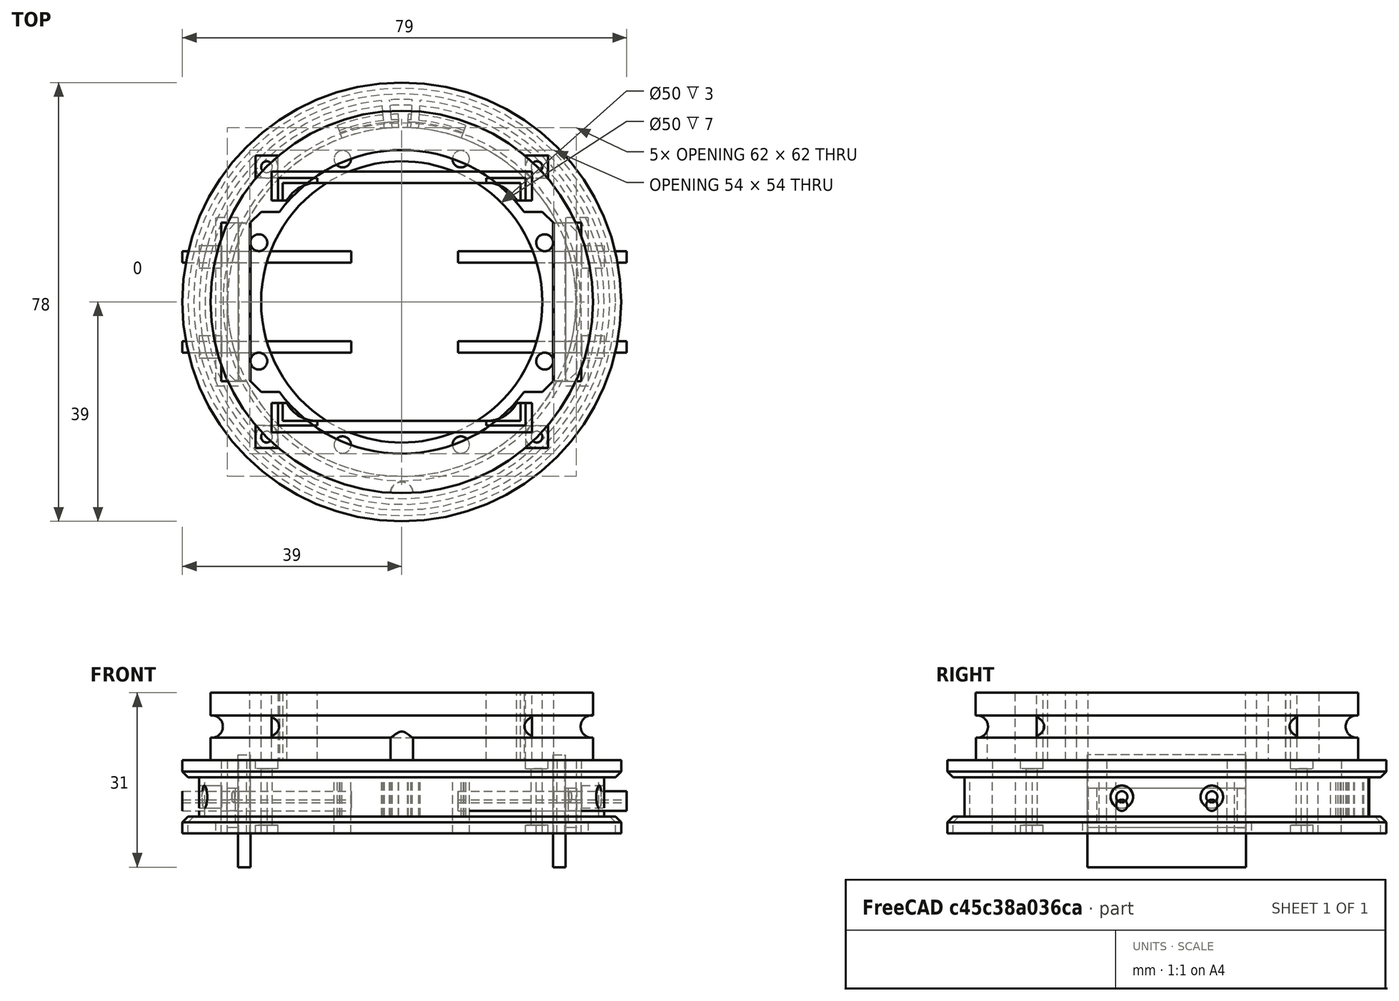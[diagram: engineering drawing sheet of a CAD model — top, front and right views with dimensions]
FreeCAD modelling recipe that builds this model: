
FCSTD DOCUMENT  (FreeCAD 0.19R24276 (Git))
Label: G-mini_encoder-ring_008
License: All rights reserved
LicenseURL: http://en.wikipedia.org/wiki/All_rights_reserved
objects: Part::Cylinder×73, Part::Box×67, Part::Cut×61, Part::Compound×53, Part::FeaturePython×11, Part::Chamfer×8, Mesh::Feature×5, Part::Torus×2
note: 275 computed .brp shape members not serialized (recipe doc carries the construction recipe); baked Part::Feature solids carry a one-line shape summary decoded from their .brp

FEATURE [Part::FeaturePython] Tube035  # WARN: FeaturePython — macro-defined, semantics opaque (R4)
  AttacherType = Attacher::AttachEngine3D
  Height = 2
  InnerRadius = 31
  OuterRadius = 39
  Placement = pos=(17,-103,10) rot=(1,0,0;1.5708rad)
FEATURE [Part::Box] Box850  label="Krychle849"
  AttacherType = Attacher::AttachEngine3D
  Height = 28
  Length = 2
  Placement = pos=(-14.1,-111,-4) rot=(0,0,1;0rad)
  Width = 7
FEATURE [Part::Box] Box851  label="Krychle850"
  AttacherType = Attacher::AttachEngine3D
  Height = 30
  Length = 4
  Placement = pos=(-16.1,-105,-5) rot=(0,0,1;0rad)
  Width = 2
FEATURE [Part::Box] Box852  label="Krychle851"
  AttacherType = Attacher::AttachEngine3D
  Height = 28.2
  Length = 2.2
  Placement = pos=(-12.1,-111,-4.1) rot=(0,0,1;0rad)
  Width = 10
FEATURE [Part::Cut] Cut807
  Base = -> Tube035
  Tool = -> Box852
FEATURE [Part::Compound] Compound985
  Links = -> [Box851,Cut807]
FEATURE [Part::Cylinder] Cylinder2203  label="Válec2203"
  Angle = 360
  AttacherType = Attacher::AttachEngine3D
  Height = 20
  Placement = pos=(-17,-108,2) rot=(0,1,0;1.5708rad)
  Radius = 1
FEATURE [Part::Cylinder] Cylinder2204  label="Válec2204"
  Angle = 360
  AttacherType = Attacher::AttachEngine3D
  Height = 20
  Placement = pos=(-17,-108,18) rot=(0,1,0;1.5708rad)
  Radius = 1
FEATURE [Part::Compound] Compound986
  Links = -> [Cylinder2203,Cylinder2204]
FEATURE [Part::Cut] Cut811
  Base = -> Box850
  Tool = -> Compound986
FEATURE [Part::Chamfer] Chamfer069
  Base = -> Cut811
  Edges = 2 edges r=1.5: [Edge2,Edge3]
FEATURE [Part::Box] Box853  label="Krychle852"
  AttacherType = Attacher::AttachEngine3D
  Height = 28.2
  Length = 2.2
  Placement = pos=(43.9,-111,-4.1) rot=(0,0,1;0rad)
  Width = 10
FEATURE [Part::Cut] Cut810
  Base = -> Compound985
  Tool = -> Box853
FEATURE [Part::Box] Box855  label="Krychle854"
  AttacherType = Attacher::AttachEngine3D
  Height = 28
  Length = 2
  Placement = pos=(46.1,-111,-4) rot=(0,0,1;0rad)
  Width = 7
FEATURE [Part::Box] Box856  label="Krychle855"
  AttacherType = Attacher::AttachEngine3D
  Height = 30
  Length = 4
  Placement = pos=(46.1,-105,-5) rot=(0,0,1;0rad)
  Width = 2
FEATURE [Part::Cylinder] Cylinder2205  label="Válec2205"
  Angle = 360
  AttacherType = Attacher::AttachEngine3D
  Height = 20
  Placement = pos=(32,-108,2) rot=(0,1,0;1.5708rad)
  Radius = 1
FEATURE [Part::Cylinder] Cylinder2206  label="Válec2206"
  Angle = 360
  AttacherType = Attacher::AttachEngine3D
  Height = 20
  Placement = pos=(32,-108,18) rot=(0,1,0;1.5708rad)
  Radius = 1
FEATURE [Part::Compound] Compound988
  Links = -> [Cylinder2205,Cylinder2206]
FEATURE [Part::Cut] Cut809
  Base = -> Box855
  Tool = -> Compound988
FEATURE [Part::Chamfer] Chamfer068
  Base = -> Cut809
  Edges = 2 edges r=1.5: [Edge11,Edge13]
FEATURE [Part::Compound] Compound989
  Links = -> [Chamfer069,Chamfer068,Cut810]
FEATURE [Part::Compound] Compound990  label="Wrist_halo-cover"
  Links = -> [Box856,Compound989]
  Placement = pos=(17,10,-111) rot=(0,0.707107,-0.707107;3.14159rad)
FEATURE [Part::FeaturePython] Tube084  # WARN: FeaturePython — macro-defined, semantics opaque (R4)
  AttacherType = Attacher::AttachEngine3D
  Height = 7
  InnerRadius = 25
  OuterRadius = 35
  Placement = pos=(0,0,3) rot=(0,0,1;0rad)
FEATURE [Part::FeaturePython] Tube093  # WARN: FeaturePython — macro-defined, semantics opaque (R4)
  AttacherType = Attacher::AttachEngine3D
  Height = 7
  InnerRadius = 31
  OuterRadius = 32.4
  Placement = pos=(0,0,-22) rot=(0,0,1;0rad)
FEATURE [Part::FeaturePython] Tube094  # WARN: FeaturePython — macro-defined, semantics opaque (R4)
  AttacherType = Attacher::AttachEngine3D
  Height = 7
  InnerRadius = 31
  OuterRadius = 32.4
  Placement = pos=(0,0,-22) rot=(0,0,1;0rad)
FEATURE [Part::Cylinder] Cylinder2439  label="Válec2425"
  Angle = 360
  AttacherType = Attacher::AttachEngine3D
  Height = 34
  Placement = pos=(0,0,-21) rot=(0,0,1;0rad)
  Radius = 25
FEATURE [Part::Cylinder] Cylinder2440  label="Válec2426"
  Angle = 360
  AttacherType = Attacher::AttachEngine3D
  Height = 3
  Radius = 38
FEATURE [Part::Cut] Cut885
  Base = -> Cylinder2440
  Tool = -> Cylinder2439
FEATURE [Part::Chamfer] Chamfer089
  Base = -> Cut885
  Edges = 1 edges r=1: [Edge1]
FEATURE [Part::Cylinder] Cylinder1833  label="Válec1833"
  Angle = 360
  AttacherType = Attacher::AttachEngine3D
  Height = 7
  Placement = pos=(0,0,-22) rot=(0,0,1;0rad)
  Radius = 31
FEATURE [Part::Box] Box736  label="Krychle736"
  AttacherType = Attacher::AttachEngine3D
  Height = 7
  Length = 1.4
  Placement = pos=(0,0,-22) rot=(0,0,-1;0.05236rad)
  Width = 60
FEATURE [Part::Box] Box737  label="Krychle737"
  AttacherType = Attacher::AttachEngine3D
  Height = 7
  Length = 1.4
  Placement = pos=(0,0,-22) rot=(0,0,1;0.099484rad)
  Width = 60
FEATURE [Part::Compound] Compound906
  Links = -> [Box736,Box737]
FEATURE [Part::Cut] Cut549
  Base = -> Compound906
  Placement = pos=(0,0,25) rot=(0,0,1;0rad)
  Tool = -> Cylinder1833
FEATURE [Part::Cut] Cut886
  Base = -> Tube084
  Tool = -> Cut549
FEATURE [Part::Box] Box731  label="Krychle731"
  AttacherType = Attacher::AttachEngine3D
  Height = 7
  Length = 60
  Placement = pos=(0,0,-22) rot=(0,0,-1;0.349066rad)
  Width = 60
FEATURE [Part::Box] Box732  label="Krychle732"
  AttacherType = Attacher::AttachEngine3D
  Height = 7
  Length = 60
  Placement = pos=(-56.3816,-20.5212,-22) rot=(0,0,1;0.349066rad)
  Width = 60
FEATURE [Part::Box] Box733  label="Krychle733"
  AttacherType = Attacher::AttachEngine3D
  Height = 7
  Length = 60
  Placement = pos=(0,0,-22) rot=(0,0,-1;0.034907rad)
  Width = 60
FEATURE [Part::Box] Box739  label="Krychle739"
  AttacherType = Attacher::AttachEngine3D
  Height = 7
  Length = 120
  Placement = pos=(-60,-60,-22) rot=(0,0,-1;0rad)
  Width = 60
FEATURE [Part::Cut] Cut560
  Base = -> Tube093
  Tool = -> Box739
FEATURE [Part::Box] Box740  label="Krychle740"
  AttacherType = Attacher::AttachEngine3D
  Height = 7
  Length = 60
  Placement = pos=(-59.9909,-1.04714,-22) rot=(0,0,1;0.017453rad)
  Width = 60
FEATURE [Part::Box] Box741  label="Krychle741"
  AttacherType = Attacher::AttachEngine3D
  Height = 7
  Length = 120
  Placement = pos=(-60,-60,-22) rot=(0,0,-1;0rad)
  Width = 60
FEATURE [Part::Cut] Cut556
  Base = -> Tube094
  Tool = -> Box741
FEATURE [Part::Compound] Compound904
  Links = -> [Box733,Box740]
FEATURE [Part::Cut] Cut555
  Base = -> Cut556
  Placement = pos=(0,0,-7) rot=(0,0,1;0rad)
  Tool = -> Compound904
FEATURE [Part::Compound] Compound908
  Links = -> [Box731,Box732]
FEATURE [Part::Cut] Cut557
  Base = -> Cut560
  Placement = pos=(0,0,-7) rot=(0,0,1;0rad)
  Tool = -> Compound908
FEATURE [Part::Cut] Cut553
  Base = -> Cut557
  Placement = pos=(0,0,32) rot=(0,0,1;0rad)
  Tool = -> Cut555
FEATURE [Part::Cut] Cut887
  Base = -> Cut886
  Tool = -> Cut553
FEATURE [Part::Compound] Compound1069  label="J-mini_encoder-belt-ring_rear1"
  Links = -> [Chamfer089,Cut887]
  Placement = pos=(0,0,-8) rot=(0,0,1;0rad)
FEATURE [Part::Cylinder] Cylinder2539  label="Válec2509"
  Angle = 360
  AttacherType = Attacher::AttachEngine3D
  Height = 20
  Placement = pos=(-27.5,-4e-15,10) rot=(0,0,1;1.5708rad)
  Radius = 1.5
FEATURE [Part::Cylinder] Cylinder2540  label="Válec2510"
  Angle = 360
  AttacherType = Attacher::AttachEngine3D
  Height = 20
  Placement = pos=(-19.4454,19.4454,10) rot=(0,0,1;0.785398rad)
  Radius = 1.5
FEATURE [Part::Cylinder] Cylinder2541  label="Válec2511"
  Angle = 360
  AttacherType = Attacher::AttachEngine3D
  Height = 20
  Placement = pos=(0,27.5,10) rot=(0,0,1;0rad)
  Radius = 1.5
FEATURE [Part::Cylinder] Cylinder2542  label="Válec2512"
  Angle = 360
  AttacherType = Attacher::AttachEngine3D
  Height = 20
  Placement = pos=(-19.4454,-19.4454,10) rot=(0,0,1;2.35619rad)
  Radius = 1.5
FEATURE [Part::Cylinder] Cylinder2543  label="Válec2513"
  Angle = 360
  AttacherType = Attacher::AttachEngine3D
  Height = 20
  Placement = pos=(27.5,1.2e-14,10) rot=(0,0,-1;1.5708rad)
  Radius = 1.5
FEATURE [Part::Cylinder] Cylinder2544  label="Válec2514"
  Angle = 360
  AttacherType = Attacher::AttachEngine3D
  Height = 20
  Placement = pos=(19.4454,-19.4454,10) rot=(0,0,1;3.92699rad)
  Radius = 1.5
FEATURE [Part::Cylinder] Cylinder2545  label="Válec2515"
  Angle = 360
  AttacherType = Attacher::AttachEngine3D
  Height = 20
  Placement = pos=(19.4454,19.4454,10) rot=(0,0,-1;0.785398rad)
  Radius = 1.5
FEATURE [Part::Cylinder] Cylinder2546  label="Válec2516"
  Angle = 360
  AttacherType = Attacher::AttachEngine3D
  Height = 20
  Placement = pos=(1.1e-14,-27.5,10) rot=(0,0,1;3.14159rad)
  Radius = 1.5
FEATURE [Part::Compound] Compound1129
  Links = -> [Cylinder2541,Cylinder2540,Cylinder2539,Cylinder2542,Cylinder2546,Cylinder2543,Cylinder2544,Cylinder2545]
  Placement = pos=(0,0,-27) rot=(0,0,1;0.392699rad)
FEATURE [Part::Cut] Cut947  label="J-mini_encoder-belt-ring_rear"
  Base = -> Compound1069
  Tool = -> Compound1129
FEATURE [Part::Cylinder] Cylinder2547  label="Válec2517"
  Angle = 360
  AttacherType = Attacher::AttachEngine3D
  Height = 30
  Placement = pos=(-17,-108,2) rot=(0,1,0;1.5708rad)
  Radius = 1
FEATURE [Part::Cylinder] Cylinder2548  label="Válec2518"
  Angle = 360
  AttacherType = Attacher::AttachEngine3D
  Height = 30
  Placement = pos=(-17,-108,18) rot=(0,1,0;1.5708rad)
  Radius = 1
FEATURE [Part::Cylinder] Cylinder2549  label="Válec2519"
  Angle = 360
  AttacherType = Attacher::AttachEngine3D
  Height = 30
  Placement = pos=(32,-108,18) rot=(0,1,0;1.5708rad)
  Radius = 1
FEATURE [Part::Cylinder] Cylinder2550  label="Válec2520"
  Angle = 360
  AttacherType = Attacher::AttachEngine3D
  Height = 30
  Placement = pos=(32,-108,2) rot=(0,1,0;1.5708rad)
  Radius = 1
FEATURE [Part::Compound] Compound
  Links = -> [Cylinder2547,Cylinder2548,Cylinder2549,Cylinder2550]
  Placement = pos=(-22,10,105) rot=(1,0,0;1.5708rad)
FEATURE [Part::Cylinder] Cylinder2551  label="Válec2521"
  Angle = 360
  AttacherType = Attacher::AttachEngine3D
  Height = 4
  Placement = pos=(-18,-106.5,2) rot=(0,1,0;1.5708rad)
  Radius = 2
FEATURE [Part::Cylinder] Cylinder2552  label="Válec2522"
  Angle = 360
  AttacherType = Attacher::AttachEngine3D
  Height = 4
  Placement = pos=(-18,-106.5,18) rot=(0,1,0;1.5708rad)
  Radius = 2
FEATURE [Part::Cylinder] Cylinder2553  label="Válec2523"
  Angle = 360
  AttacherType = Attacher::AttachEngine3D
  Height = 4
  Placement = pos=(50,-106.5,18) rot=(0,1,0;1.5708rad)
  Radius = 2
FEATURE [Part::Cylinder] Cylinder2554  label="Válec2524"
  Angle = 360
  AttacherType = Attacher::AttachEngine3D
  Height = 4
  Placement = pos=(50,-106.5,2) rot=(0,1,0;1.5708rad)
  Radius = 2
FEATURE [Part::Compound] Compound1130
  Links = -> [Cylinder2551,Cylinder2552,Cylinder2553,Cylinder2554]
  Placement = pos=(-18,10,105) rot=(1,0,0;1.5708rad)
FEATURE [Part::Box] Box857  label="Krychle856"
  AttacherType = Attacher::AttachEngine3D
  Height = 28.2
  Length = 2.2
  Placement = pos=(-12.1,-111,-4.1) rot=(0,0,1;0rad)
  Width = 20
FEATURE [Part::Box] Box858  label="Krychle857"
  AttacherType = Attacher::AttachEngine3D
  Height = 28.2
  Length = 2.2
  Placement = pos=(43.9,-111,-4.1) rot=(0,0,1;0rad)
  Width = 20
FEATURE [Part::Compound] Compound1131
  Links = -> [Box857,Box858]
  Placement = pos=(-17,10,97) rot=(1,0,0;1.5708rad)
FEATURE [Part::Cylinder] Cylinder2555  label="Válec2525"
  Angle = 360
  AttacherType = Attacher::AttachEngine3D
  Height = 34
  Placement = pos=(0,0,-21) rot=(0,0,1;0rad)
  Radius = 31
FEATURE [Part::Cylinder] Cylinder2556  label="Válec2526"
  Angle = 360
  AttacherType = Attacher::AttachEngine3D
  Height = 3
  Radius = 39
FEATURE [Part::Cut] Cut948
  Base = -> Cylinder2556
  Tool = -> Cylinder2555
FEATURE [Part::Chamfer] Chamfer090
  Base = -> Cut948
  Edges = 1 edges r=1: [Edge1]
  Placement = pos=(0,0,-8) rot=(0,0,1;0rad)
FEATURE [Part::FeaturePython] Tube095  # WARN: FeaturePython — macro-defined, semantics opaque (R4)
  AttacherType = Attacher::AttachEngine3D
  Height = 7
  InnerRadius = 31
  OuterRadius = 36
  Placement = pos=(0,0,3) rot=(0,0,1;0rad)
FEATURE [Part::FeaturePython] Tube096  # WARN: FeaturePython — macro-defined, semantics opaque (R4)
  AttacherType = Attacher::AttachEngine3D
  Height = 7
  InnerRadius = 32
  OuterRadius = 33.4
  Placement = pos=(0,0,-22) rot=(0,0,1;0rad)
FEATURE [Part::FeaturePython] Tube097  # WARN: FeaturePython — macro-defined, semantics opaque (R4)
  AttacherType = Attacher::AttachEngine3D
  Height = 7
  InnerRadius = 32
  OuterRadius = 33.4
  Placement = pos=(0,0,-22) rot=(0,0,1;0rad)
FEATURE [Part::Cylinder] Cylinder2557  label="Válec2527"
  Angle = 360
  AttacherType = Attacher::AttachEngine3D
  Height = 7
  Placement = pos=(0,0,-22) rot=(0,0,1;0rad)
  Radius = 31
FEATURE [Part::Box] Box859  label="Krychle858"
  AttacherType = Attacher::AttachEngine3D
  Height = 7
  Length = 1.4
  Placement = pos=(0,0,-22) rot=(0,0,-1;0.05236rad)
  Width = 60
FEATURE [Part::Box] Box860  label="Krychle859"
  AttacherType = Attacher::AttachEngine3D
  Height = 7
  Length = 1.4
  Placement = pos=(0,0,-22) rot=(0,0,1;0.099484rad)
  Width = 60
FEATURE [Part::Compound] Compound1132
  Links = -> [Box859,Box860]
FEATURE [Part::Cut] Cut949
  Base = -> Compound1132
  Placement = pos=(0,0,25) rot=(0,0,1;0rad)
  Tool = -> Cylinder2557
FEATURE [Part::Cut] Cut953
  Base = -> Tube095
  Tool = -> Cut949
FEATURE [Part::Box] Box861  label="Krychle860"
  AttacherType = Attacher::AttachEngine3D
  Height = 7
  Length = 60
  Placement = pos=(0,0,-22) rot=(0,0,-1;0.349066rad)
  Width = 60
FEATURE [Part::Box] Box862  label="Krychle861"
  AttacherType = Attacher::AttachEngine3D
  Height = 7
  Length = 60
  Placement = pos=(-56.3816,-20.5212,-22) rot=(0,0,1;0.349066rad)
  Width = 60
FEATURE [Part::Compound] Compound1134
  Links = -> [Box861,Box862]
FEATURE [Part::Box] Box863  label="Krychle862"
  AttacherType = Attacher::AttachEngine3D
  Height = 7
  Length = 60
  Placement = pos=(0,0,-22) rot=(0,0,-1;0.034907rad)
  Width = 60
FEATURE [Part::Box] Box864  label="Krychle863"
  AttacherType = Attacher::AttachEngine3D
  Height = 7
  Length = 120
  Placement = pos=(-60,-60,-22) rot=(0,0,-1;0rad)
  Width = 60
FEATURE [Part::Cut] Cut952
  Base = -> Tube096
  Tool = -> Box864
FEATURE [Part::Cut] Cut951
  Base = -> Cut952
  Placement = pos=(0,0,-7) rot=(0,0,1;0rad)
  Tool = -> Compound1134
FEATURE [Part::Box] Box865  label="Krychle864"
  AttacherType = Attacher::AttachEngine3D
  Height = 7
  Length = 60
  Placement = pos=(-59.9909,-1.04714,-22) rot=(0,0,1;0.017453rad)
  Width = 60
FEATURE [Part::Compound] Compound1133
  Links = -> [Box863,Box865]
FEATURE [Part::Box] Box866  label="Krychle865"
  AttacherType = Attacher::AttachEngine3D
  Height = 7
  Length = 120
  Placement = pos=(-60,-60,-22) rot=(0,0,-1;0rad)
  Width = 60
FEATURE [Part::Cut] Cut956
  Base = -> Tube097
  Tool = -> Box866
FEATURE [Part::Cut] Cut955
  Base = -> Cut956
  Placement = pos=(0,0,-7) rot=(0,0,1;0rad)
  Tool = -> Compound1133
FEATURE [Part::Cut] Cut950
  Base = -> Cut951
  Placement = pos=(0,0,32) rot=(0,0,1;0rad)
  Tool = -> Cut955
FEATURE [Part::Cut] Cut954
  Base = -> Cut953
  Placement = pos=(0,0,-8) rot=(0,0,1;0rad)
  Tool = -> Cut950
FEATURE [Part::FeaturePython] Tube098  # WARN: FeaturePython — macro-defined, semantics opaque (R4)
  AttacherType = Attacher::AttachEngine3D
  Height = 7
  InnerRadius = 31
  OuterRadius = 36
  Placement = pos=(0,0,3) rot=(0,0,1;0rad)
FEATURE [Part::FeaturePython] Tube099  # WARN: FeaturePython — macro-defined, semantics opaque (R4)
  AttacherType = Attacher::AttachEngine3D
  Height = 7
  InnerRadius = 32
  OuterRadius = 33.4
  Placement = pos=(0,0,-22) rot=(0,0,1;0rad)
FEATURE [Part::FeaturePython] Tube100  # WARN: FeaturePython — macro-defined, semantics opaque (R4)
  AttacherType = Attacher::AttachEngine3D
  Height = 7
  InnerRadius = 32
  OuterRadius = 33.4
  Placement = pos=(0,0,-22) rot=(0,0,1;0rad)
FEATURE [Part::Cylinder] Cylinder2558  label="Válec2528"
  Angle = 360
  AttacherType = Attacher::AttachEngine3D
  Height = 7
  Placement = pos=(0,0,-22) rot=(0,0,1;0rad)
  Radius = 32
FEATURE [Part::Box] Box867  label="Krychle866"
  AttacherType = Attacher::AttachEngine3D
  Height = 7
  Length = 1.4
  Placement = pos=(0,0,-22) rot=(0,0,-1;0.05236rad)
  Width = 60
FEATURE [Part::Box] Box868  label="Krychle867"
  AttacherType = Attacher::AttachEngine3D
  Height = 7
  Length = 1.4
  Placement = pos=(0,0,-22) rot=(0,0,1;0.099484rad)
  Width = 60
FEATURE [Part::Compound] Compound1135
  Links = -> [Box867,Box868]
FEATURE [Part::Cut] Cut957
  Base = -> Compound1135
  Placement = pos=(0,0,25) rot=(0,0,1;0rad)
  Tool = -> Cylinder2558
FEATURE [Part::Cut] Cut961
  Base = -> Tube098
  Tool = -> Cut957
FEATURE [Part::Box] Box869  label="Krychle868"
  AttacherType = Attacher::AttachEngine3D
  Height = 7
  Length = 60
  Placement = pos=(0,0,-22) rot=(0,0,-1;0.349066rad)
  Width = 60
FEATURE [Part::Box] Box870  label="Krychle869"
  AttacherType = Attacher::AttachEngine3D
  Height = 7
  Length = 60
  Placement = pos=(-56.3816,-20.5212,-22) rot=(0,0,1;0.349066rad)
  Width = 60
FEATURE [Part::Compound] Compound1137
  Links = -> [Box869,Box870]
FEATURE [Part::Box] Box871  label="Krychle870"
  AttacherType = Attacher::AttachEngine3D
  Height = 7
  Length = 60
  Placement = pos=(0,0,-22) rot=(0,0,-1;0.034907rad)
  Width = 60
FEATURE [Part::Box] Box872  label="Krychle871"
  AttacherType = Attacher::AttachEngine3D
  Height = 7
  Length = 120
  Placement = pos=(-60,-60,-22) rot=(0,0,-1;0rad)
  Width = 60
FEATURE [Part::Cut] Cut960
  Base = -> Tube099
  Tool = -> Box872
FEATURE [Part::Cut] Cut959
  Base = -> Cut960
  Placement = pos=(0,0,-7) rot=(0,0,1;0rad)
  Tool = -> Compound1137
FEATURE [Part::Box] Box873  label="Krychle872"
  AttacherType = Attacher::AttachEngine3D
  Height = 7
  Length = 60
  Placement = pos=(-59.9909,-1.04714,-22) rot=(0,0,1;0.017453rad)
  Width = 60
FEATURE [Part::Compound] Compound1136
  Links = -> [Box871,Box873]
FEATURE [Part::Box] Box874  label="Krychle873"
  AttacherType = Attacher::AttachEngine3D
  Height = 7
  Length = 120
  Placement = pos=(-60,-60,-22) rot=(0,0,-1;0rad)
  Width = 60
FEATURE [Part::Cut] Cut964
  Base = -> Tube100
  Tool = -> Box874
FEATURE [Part::Cut] Cut963
  Base = -> Cut964
  Placement = pos=(0,0,-7) rot=(0,0,1;0rad)
  Tool = -> Compound1136
FEATURE [Part::Cut] Cut958
  Base = -> Cut959
  Placement = pos=(0,0,32) rot=(0,0,1;0rad)
  Tool = -> Cut963
FEATURE [Part::Cut] Cut962
  Base = -> Cut961
  Placement = pos=(0,0,-8) rot=(0,0,1;0rad)
  Tool = -> Cut958
FEATURE [Part::Box] Box875  label="Krychle874"
  AttacherType = Attacher::AttachEngine3D
  Height = 28.2
  Length = 2.2
  Placement = pos=(-12.1,-111,-4.1) rot=(0,0,1;0rad)
  Width = 20
FEATURE [Part::Box] Box876  label="Krychle875"
  AttacherType = Attacher::AttachEngine3D
  Height = 28.2
  Length = 2.2
  Placement = pos=(43.9,-111,-4.1) rot=(0,0,1;0rad)
  Width = 20
FEATURE [Part::Compound] Compound1138
  Links = -> [Box875,Box876]
  Placement = pos=(-17,10,97) rot=(1,0,0;1.5708rad)
FEATURE [Part::Box] Box877  label="Krychle876"
  AttacherType = Attacher::AttachEngine3D
  Height = 28.2
  Length = 2.2
  Placement = pos=(-12.1,-111,-4.1) rot=(0,0,1;0rad)
  Width = 20
FEATURE [Part::Box] Box878  label="Krychle877"
  AttacherType = Attacher::AttachEngine3D
  Height = 28.2
  Length = 2.2
  Placement = pos=(43.9,-111,-4.1) rot=(0,0,1;0rad)
  Width = 20
FEATURE [Part::Compound] Compound1139
  Links = -> [Box877,Box878]
  Placement = pos=(-17,10,97) rot=(1,0,0;1.5708rad)
FEATURE [Part::Cut] Cut
  Base = -> Cut962
  Tool = -> Compound1138
FEATURE [Part::Cut] Cut965
  Base = -> Chamfer090
  Tool = -> Compound1139
FEATURE [Part::Box] Box879  label="Krychle878"
  AttacherType = Attacher::AttachEngine3D
  Height = 28.2
  Length = 5
  Placement = pos=(-15.1,-108,-4.1) rot=(0,0,1;0rad)
  Width = 7
FEATURE [Part::Box] Box880  label="Krychle879"
  AttacherType = Attacher::AttachEngine3D
  Height = 28.2
  Length = 5
  Placement = pos=(43.9,-108,-4.1) rot=(0,0,1;0rad)
  Width = 7
FEATURE [Part::Compound] Compound1140
  Links = -> [Box879,Box880]
  Placement = pos=(-17,10,103) rot=(1,0,0;1.5708rad)
FEATURE [Part::Box] Box881  label="Krychle880"
  AttacherType = Attacher::AttachEngine3D
  Height = 28.2
  Length = 2.2
  Placement = pos=(-12.1,-111,-4.1) rot=(0,0,1;0rad)
  Width = 20
FEATURE [Part::Box] Box882  label="Krychle881"
  AttacherType = Attacher::AttachEngine3D
  Height = 28.2
  Length = 2.2
  Placement = pos=(43.9,-111,-4.1) rot=(0,0,1;0rad)
  Width = 20
FEATURE [Part::Compound] Compound1141
  Links = -> [Box881,Box882]
  Placement = pos=(-17,10,97) rot=(1,0,0;1.5708rad)
FEATURE [Part::Cut] Cut966
  Base = -> Compound1140
  Tool = -> Compound1141
FEATURE [Part::Cylinder] Cylinder2559  label="Válec2529"
  Angle = 360
  AttacherType = Attacher::AttachEngine3D
  Height = 30
  Placement = pos=(-17,-108,2) rot=(0,1,0;1.5708rad)
  Radius = 1
FEATURE [Part::Cylinder] Cylinder2560  label="Válec2530"
  Angle = 360
  AttacherType = Attacher::AttachEngine3D
  Height = 30
  Placement = pos=(-17,-108,18) rot=(0,1,0;1.5708rad)
  Radius = 1
FEATURE [Part::Cylinder] Cylinder2561  label="Válec2531"
  Angle = 360
  AttacherType = Attacher::AttachEngine3D
  Height = 30
  Placement = pos=(32,-108,18) rot=(0,1,0;1.5708rad)
  Radius = 1
FEATURE [Part::Cylinder] Cylinder2562  label="Válec2532"
  Angle = 360
  AttacherType = Attacher::AttachEngine3D
  Height = 30
  Placement = pos=(32,-108,2) rot=(0,1,0;1.5708rad)
  Radius = 1
FEATURE [Part::Compound] Compound1142
  Links = -> [Cylinder2559,Cylinder2560,Cylinder2561,Cylinder2562]
  Placement = pos=(-22,10,106.5) rot=(1,0,0;1.5708rad)
FEATURE [Part::Cut] Cut967
  Base = -> Cut966
  Tool = -> Compound1142
FEATURE [Part::Cylinder] Cylinder2563  label="Válec2533"
  Angle = 360
  AttacherType = Attacher::AttachEngine3D
  Height = 30
  Placement = pos=(-17,-108,2) rot=(0,1,0;1.5708rad)
  Radius = 1
FEATURE [Part::Cylinder] Cylinder2564  label="Válec2534"
  Angle = 360
  AttacherType = Attacher::AttachEngine3D
  Height = 30
  Placement = pos=(-17,-108,18) rot=(0,1,0;1.5708rad)
  Radius = 1
FEATURE [Part::Cylinder] Cylinder2565  label="Válec2535"
  Angle = 360
  AttacherType = Attacher::AttachEngine3D
  Height = 30
  Placement = pos=(32,-108,18) rot=(0,1,0;1.5708rad)
  Radius = 1
FEATURE [Part::Cylinder] Cylinder2566  label="Válec2536"
  Angle = 360
  AttacherType = Attacher::AttachEngine3D
  Height = 30
  Placement = pos=(32,-108,2) rot=(0,1,0;1.5708rad)
  Radius = 1
FEATURE [Part::Compound] Compound1143
  Links = -> [Cylinder2563,Cylinder2564,Cylinder2565,Cylinder2566]
  Placement = pos=(-22,10,106.5) rot=(1,0,0;1.5708rad)
FEATURE [Part::Cut] Cut968
  Base = -> Cut
  Tool = -> Compound1143
FEATURE [Part::Cylinder] Cylinder2567  label="Válec2537"
  Angle = 360
  AttacherType = Attacher::AttachEngine3D
  Height = 4
  Placement = pos=(-18,-106.5,2) rot=(0,1,0;1.5708rad)
  Radius = 2
FEATURE [Part::Cylinder] Cylinder2568  label="Válec2538"
  Angle = 360
  AttacherType = Attacher::AttachEngine3D
  Height = 4
  Placement = pos=(-18,-106.5,18) rot=(0,1,0;1.5708rad)
  Radius = 2
FEATURE [Part::Cylinder] Cylinder2569  label="Válec2539"
  Angle = 360
  AttacherType = Attacher::AttachEngine3D
  Height = 4
  Placement = pos=(50,-106.5,18) rot=(0,1,0;1.5708rad)
  Radius = 2
FEATURE [Part::Cylinder] Cylinder2570  label="Válec2540"
  Angle = 360
  AttacherType = Attacher::AttachEngine3D
  Height = 4
  Placement = pos=(50,-106.5,2) rot=(0,1,0;1.5708rad)
  Radius = 2
FEATURE [Part::Compound] Compound1144
  Links = -> [Cylinder2567,Cylinder2568,Cylinder2569,Cylinder2570]
  Placement = pos=(-18,10,105) rot=(1,0,0;1.5708rad)
FEATURE [Part::Cut] Cut969
  Base = -> Cut968
  Tool = -> Compound1144
FEATURE [Part::Cut] Cut970
  Base = -> Cut967
  Tool = -> Compound1130
FEATURE [Part::Cylinder] Cylinder2571  label="Válec2541"
  Angle = 360
  AttacherType = Attacher::AttachEngine3D
  Height = 34
  Placement = pos=(0,0,-21) rot=(0,0,1;0rad)
  Radius = 31
FEATURE [Part::Cylinder] Cylinder2572  label="Válec2542"
  Angle = 360
  AttacherType = Attacher::AttachEngine3D
  Height = 3
  Radius = 39
FEATURE [Part::Cut] Cut971
  Base = -> Cylinder2572
  Tool = -> Cylinder2571
FEATURE [Part::Chamfer] Chamfer091
  Base = -> Cut971
  Edges = 1 edges r=1: [Edge1]
  Placement = pos=(0,0,-8) rot=(0,0,1;0rad)
FEATURE [Part::Box] Box883  label="Krychle882"
  AttacherType = Attacher::AttachEngine3D
  Height = 28.2
  Length = 2.2
  Placement = pos=(-12.1,-111,-4.1) rot=(0,0,1;0rad)
  Width = 20
FEATURE [Part::Box] Box884  label="Krychle883"
  AttacherType = Attacher::AttachEngine3D
  Height = 28.2
  Length = 2.2
  Placement = pos=(43.9,-111,-4.1) rot=(0,0,1;0rad)
  Width = 20
FEATURE [Part::Compound] Compound1145
  Links = -> [Box883,Box884]
  Placement = pos=(-17,10,97) rot=(1,0,0;1.5708rad)
FEATURE [Part::Cut] Cut972
  Base = -> Chamfer091
  Tool = -> Compound1145
FEATURE [Part::Cylinder] Cylinder2573  label="Válec2543"
  Angle = 360
  AttacherType = Attacher::AttachEngine3D
  Height = 4
  Placement = pos=(-18,-106.5,2) rot=(0,1,0;1.5708rad)
  Radius = 2
FEATURE [Part::Cylinder] Cylinder2574  label="Válec2544"
  Angle = 360
  AttacherType = Attacher::AttachEngine3D
  Height = 4
  Placement = pos=(-18,-106.5,18) rot=(0,1,0;1.5708rad)
  Radius = 2
FEATURE [Part::Cylinder] Cylinder2575  label="Válec2545"
  Angle = 360
  AttacherType = Attacher::AttachEngine3D
  Height = 4
  Placement = pos=(50,-106.5,18) rot=(0,1,0;1.5708rad)
  Radius = 2
FEATURE [Part::Cylinder] Cylinder2576  label="Válec2546"
  Angle = 360
  AttacherType = Attacher::AttachEngine3D
  Height = 4
  Placement = pos=(50,-106.5,2) rot=(0,1,0;1.5708rad)
  Radius = 2
FEATURE [Part::Compound] Compound1149
  Links = -> [Cylinder2573,Cylinder2574,Cylinder2575,Cylinder2576]
  Placement = pos=(-18,10,105) rot=(1,0,0;1.5708rad)
FEATURE [Part::Box] Box885  label="Krychle884"
  AttacherType = Attacher::AttachEngine3D
  Height = 28.2
  Length = 5
  Placement = pos=(-15.1,-111,-4.1) rot=(0,0,1;0rad)
  Width = 3
FEATURE [Part::Box] Box886  label="Krychle885"
  AttacherType = Attacher::AttachEngine3D
  Height = 28.2
  Length = 5
  Placement = pos=(43.9,-111,-4.1) rot=(0,0,1;0rad)
  Width = 3
FEATURE [Part::Compound] Compound1148
  Links = -> [Box885,Box886]
  Placement = pos=(-17,10,103) rot=(1,0,0;1.5708rad)
FEATURE [Part::Box] Box887  label="Krychle886"
  AttacherType = Attacher::AttachEngine3D
  Height = 28.2
  Length = 2.2
  Placement = pos=(-12.1,-111,-4.1) rot=(0,0,1;0rad)
  Width = 20
FEATURE [Part::Box] Box888  label="Krychle887"
  AttacherType = Attacher::AttachEngine3D
  Height = 28.2
  Length = 2.2
  Placement = pos=(43.9,-111,-4.1) rot=(0,0,1;0rad)
  Width = 20
FEATURE [Part::Compound] Compound1146
  Links = -> [Box887,Box888]
  Placement = pos=(-17,10,97) rot=(1,0,0;1.5708rad)
FEATURE [Part::Cut] Cut975
  Base = -> Compound1148
  Tool = -> Compound1146
FEATURE [Part::Cylinder] Cylinder2577  label="Válec2547"
  Angle = 360
  AttacherType = Attacher::AttachEngine3D
  Height = 30
  Placement = pos=(-17,-108,2) rot=(0,1,0;1.5708rad)
  Radius = 1
FEATURE [Part::Cylinder] Cylinder2578  label="Válec2548"
  Angle = 360
  AttacherType = Attacher::AttachEngine3D
  Height = 30
  Placement = pos=(-17,-108,18) rot=(0,1,0;1.5708rad)
  Radius = 1
FEATURE [Part::Cylinder] Cylinder2579  label="Válec2549"
  Angle = 360
  AttacherType = Attacher::AttachEngine3D
  Height = 30
  Placement = pos=(32,-108,18) rot=(0,1,0;1.5708rad)
  Radius = 1
FEATURE [Part::Cylinder] Cylinder2580  label="Válec2550"
  Angle = 360
  AttacherType = Attacher::AttachEngine3D
  Height = 30
  Placement = pos=(32,-108,2) rot=(0,1,0;1.5708rad)
  Radius = 1
FEATURE [Part::Compound] Compound1147
  Links = -> [Cylinder2577,Cylinder2578,Cylinder2579,Cylinder2580]
  Placement = pos=(-22,10,106.5) rot=(1,0,0;1.5708rad)
FEATURE [Part::Compound] Compound1150
  Links = -> [Cut969,Cut970]
FEATURE [Part::Compound] Compound1151
  Links = -> [Cut972,Cut975]
FEATURE [Part::Cylinder] Cylinder2581  label="Válec2551"
  Angle = 360
  AttacherType = Attacher::AttachEngine3D
  Height = 34
  Placement = pos=(0,0,-21) rot=(0,0,1;0rad)
  Radius = 31
FEATURE [Part::Cylinder] Cylinder2582  label="Válec2552"
  Angle = 360
  AttacherType = Attacher::AttachEngine3D
  Height = 3
  Radius = 39
FEATURE [Part::Cut] Cut976
  Base = -> Cylinder2582
  Tool = -> Cylinder2581
FEATURE [Part::Box] Box889  label="Krychle888"
  AttacherType = Attacher::AttachEngine3D
  Height = 28.2
  Length = 2.2
  Placement = pos=(-12.1,-111,-4.1) rot=(0,0,1;0rad)
  Width = 20
FEATURE [Part::Box] Box890  label="Krychle889"
  AttacherType = Attacher::AttachEngine3D
  Height = 28.2
  Length = 2.2
  Placement = pos=(43.9,-111,-4.1) rot=(0,0,1;0rad)
  Width = 20
FEATURE [Part::Compound] Compound1153
  Links = -> [Box889,Box890]
  Placement = pos=(-17,10,97) rot=(1,0,0;1.5708rad)
FEATURE [Part::Box] Box891  label="Krychle890"
  AttacherType = Attacher::AttachEngine3D
  Height = 28.2
  Length = 5
  Placement = pos=(-15.1,-111,-4.1) rot=(0,0,1;0rad)
  Width = 3
FEATURE [Part::Box] Box892  label="Krychle891"
  AttacherType = Attacher::AttachEngine3D
  Height = 28.2
  Length = 5
  Placement = pos=(43.9,-111,-4.1) rot=(0,0,1;0rad)
  Width = 3
FEATURE [Part::Compound] Compound1155
  Links = -> [Box891,Box892]
  Placement = pos=(-17,10,103) rot=(1,0,0;1.5708rad)
FEATURE [Part::Box] Box893  label="Krychle892"
  AttacherType = Attacher::AttachEngine3D
  Height = 28.2
  Length = 2.2
  Placement = pos=(-12.1,-111,-4.1) rot=(0,0,1;0rad)
  Width = 20
FEATURE [Part::Box] Box894  label="Krychle893"
  AttacherType = Attacher::AttachEngine3D
  Height = 28.2
  Length = 2.2
  Placement = pos=(43.9,-111,-4.1) rot=(0,0,1;0rad)
  Width = 20
FEATURE [Part::Compound] Compound1154
  Links = -> [Box893,Box894]
  Placement = pos=(-17,10,97) rot=(1,0,0;1.5708rad)
FEATURE [Part::Cut] Cut978
  Base = -> Compound1155
  Tool = -> Compound1154
FEATURE [Part::Chamfer] Chamfer092
  Base = -> Cut976
  Edges = 1 edges r=1: [Edge1]
  Placement = pos=(0,0,-8) rot=(0,0,1;0rad)
FEATURE [Part::Cut] Cut977
  Base = -> Chamfer092
  Tool = -> Compound1153
FEATURE [Part::Compound] Compound1152
  Links = -> [Cut977,Cut978]
  Placement = pos=(0,0,-3) rot=(1,0,0;3.14159rad)
FEATURE [Part::Cylinder] Cylinder  label="Válec"
  Angle = 360
  AttacherType = Attacher::AttachEngine3D
  Height = 20
  Placement = pos=(24,24,-12) rot=(0,0,1;0rad)
  Radius = 1
FEATURE [Part::Box] Box  label="Krychle"
  AttacherType = Attacher::AttachEngine3D
  Height = 1.5
  Length = 4
  Placement = pos=(22,22,3) rot=(0,0,1;0rad)
  Width = 4
FEATURE [Part::Cylinder] Cylinder2583  label="Válec2553"
  Angle = 360
  AttacherType = Attacher::AttachEngine3D
  Height = 1.5
  Placement = pos=(24,24,-8) rot=(0,0,1;0rad)
  Radius = 2
FEATURE [Part::Cylinder] Cylinder2584  label="Válec2554"
  Angle = 360
  AttacherType = Attacher::AttachEngine3D
  Height = 1.5
  Placement = pos=(-24,24,-8) rot=(0,0,1;1.5708rad)
  Radius = 2
FEATURE [Part::Cylinder] Cylinder2585  label="Válec2555"
  Angle = 360
  AttacherType = Attacher::AttachEngine3D
  Height = 1.5
  Placement = pos=(-24,-24,-8) rot=(0,0,1;3.14159rad)
  Radius = 2
FEATURE [Part::Cylinder] Cylinder2586  label="Válec2556"
  Angle = 360
  AttacherType = Attacher::AttachEngine3D
  Height = 1.5
  Placement = pos=(24,-24,-8) rot=(0,0,-1;1.5708rad)
  Radius = 2
FEATURE [Part::Compound] Compound1156
  Links = -> [Cylinder2583,Cylinder2584,Cylinder2585,Cylinder2586]
FEATURE [Part::Box] Box895  label="Krychle894"
  AttacherType = Attacher::AttachEngine3D
  Height = 1.5
  Length = 4
  Placement = pos=(-22,22,3) rot=(0,0,1;1.5708rad)
  Width = 4
FEATURE [Part::Box] Box896  label="Krychle895"
  AttacherType = Attacher::AttachEngine3D
  Height = 1.5
  Length = 4
  Placement = pos=(-22,-22,3) rot=(0,0,1;3.14159rad)
  Width = 4
FEATURE [Part::Box] Box897  label="Krychle896"
  AttacherType = Attacher::AttachEngine3D
  Height = 1.5
  Length = 4
  Placement = pos=(22,-22,3) rot=(0,0,-1;1.5708rad)
  Width = 4
FEATURE [Part::Compound] Compound1157
  Links = -> [Box,Box895,Box896,Box897]
  Placement = pos=(0,0,0.5) rot=(0,0,1;0rad)
FEATURE [Part::Cylinder] Cylinder2587  label="Válec2557"
  Angle = 360
  AttacherType = Attacher::AttachEngine3D
  Height = 20
  Placement = pos=(-24,24,-12) rot=(0,0,1;1.5708rad)
  Radius = 1
FEATURE [Part::Cylinder] Cylinder2588  label="Válec2558"
  Angle = 360
  AttacherType = Attacher::AttachEngine3D
  Height = 20
  Placement = pos=(-24,-24,-12) rot=(0,0,1;3.14159rad)
  Radius = 1
FEATURE [Part::Cylinder] Cylinder2589  label="Válec2559"
  Angle = 360
  AttacherType = Attacher::AttachEngine3D
  Height = 20
  Placement = pos=(24,-24,-12) rot=(0,0,-1;1.5708rad)
  Radius = 1
FEATURE [Part::Compound] Compound1158
  Links = -> [Cylinder,Cylinder2587,Cylinder2588,Cylinder2589]
FEATURE [Part::Cut] Cut979
  Base = -> Compound1152
  Tool = -> Compound1157
FEATURE [Part::Cylinder] Cylinder2590  label="Válec2560"
  Angle = 360
  AttacherType = Attacher::AttachEngine3D
  Height = 20
  Placement = pos=(24,24,-12) rot=(0,0,1;0rad)
  Radius = 1
FEATURE [Part::Cylinder] Cylinder2591  label="Válec2561"
  Angle = 360
  AttacherType = Attacher::AttachEngine3D
  Height = 20
  Placement = pos=(-24,24,-12) rot=(0,0,1;1.5708rad)
  Radius = 1
FEATURE [Part::Cylinder] Cylinder2592  label="Válec2562"
  Angle = 360
  AttacherType = Attacher::AttachEngine3D
  Height = 20
  Placement = pos=(-24,-24,-12) rot=(0,0,1;3.14159rad)
  Radius = 1
FEATURE [Part::Cylinder] Cylinder2593  label="Válec2563"
  Angle = 360
  AttacherType = Attacher::AttachEngine3D
  Height = 20
  Placement = pos=(24,-24,-12) rot=(0,0,-1;1.5708rad)
  Radius = 1
FEATURE [Part::Compound] Compound1159
  Links = -> [Cylinder2590,Cylinder2591,Cylinder2592,Cylinder2593]
FEATURE [Part::Cut] Cut980
  Base = -> Cut979
  Tool = -> Compound1159
FEATURE [Part::Cut] Cut981
  Base = -> Compound1150
  Tool = -> Compound1158
FEATURE [Part::Cylinder] Cylinder2594  label="Válec2564"
  Angle = 360
  AttacherType = Attacher::AttachEngine3D
  Height = 20
  Placement = pos=(24,24,-12) rot=(0,0,1;0rad)
  Radius = 1
FEATURE [Part::Cylinder] Cylinder2595  label="Válec2565"
  Angle = 360
  AttacherType = Attacher::AttachEngine3D
  Height = 20
  Placement = pos=(-24,24,-12) rot=(0,0,1;1.5708rad)
  Radius = 1
FEATURE [Part::Cylinder] Cylinder2596  label="Válec2566"
  Angle = 360
  AttacherType = Attacher::AttachEngine3D
  Height = 20
  Placement = pos=(-24,-24,-12) rot=(0,0,1;3.14159rad)
  Radius = 1
FEATURE [Part::Cylinder] Cylinder2597  label="Válec2567"
  Angle = 360
  AttacherType = Attacher::AttachEngine3D
  Height = 20
  Placement = pos=(24,-24,-12) rot=(0,0,-1;1.5708rad)
  Radius = 1
FEATURE [Part::Compound] Compound1160
  Links = -> [Cylinder2594,Cylinder2595,Cylinder2596,Cylinder2597]
FEATURE [Part::Cut] Cut982
  Base = -> Compound1151
  Tool = -> Compound1160
FEATURE [Part::Cut] Cut983  label="G-mini_encoder-ring-cover"
  Base = -> Cut982
  Tool = -> Compound1156
FEATURE [Part::Compound] Compound1161  label="G-mini_encoder-belt-ring"
  Links = -> [Cut980,Cut981]
FEATURE [Part::Torus] Torus001  label="Anuloid001"
  Angle1 = -180
  Angle2 = 180
  Angle3 = 360
  AttacherType = Attacher::AttachEngine3D
  Placement = pos=(17,-98,10) rot=(1,0,0;1.5708rad)
  Radius1 = 33.8
  Radius2 = 2
FEATURE [Part::Torus] Torus  label="Anuloid"
  Angle1 = -180
  Angle2 = 180
  Angle3 = 360
  AttacherType = Attacher::AttachEngine3D
  Placement = pos=(17,-98,10) rot=(1,0,0;1.5708rad)
  Radius1 = 33.8
  Radius2 = 2
FEATURE [Part::Box] Box326  label="Krychle326"
  AttacherType = Attacher::AttachEngine3D
  Height = 32
  Length = 5.85
  Placement = pos=(-10,-134,-6) rot=(0,0,1;0rad)
  Width = 56
FEATURE [Part::FeaturePython] Tube017  # WARN: FeaturePython — macro-defined, semantics opaque (R4)
  AttacherType = Attacher::AttachEngine3D
  Height = 12
  InnerRadius = 27
  OuterRadius = 34
  Placement = pos=(17,-92,10) rot=(1,0,0;1.5708rad)
FEATURE [Part::Box] Box327  label="Krychle327"
  AttacherType = Attacher::AttachEngine3D
  Height = 32
  Length = 5.85
  Placement = pos=(38.15,-134,-6) rot=(0,0,1;0rad)
  Width = 56
FEATURE [Part::Compound] Compound248
  Links = -> [Box326,Box327]
FEATURE [Part::Chamfer] Chamfer051
  Base = -> Compound248
  Edges = 2 edges r=2: [Edge2,Edge4]
FEATURE [Part::Chamfer] Chamfer052
  Base = -> Chamfer051
  Edges = 2 edges r=2: [Edge24,Edge26]
FEATURE [Part::Cut] Cut301
  Base = -> Tube017
  Tool = -> Chamfer052
FEATURE [Part::Box] Box332  label="Krychle332"
  AttacherType = Attacher::AttachEngine3D
  Height = 12
  Length = 46.3
  Placement = pos=(-23.15,-23.15,-70) rot=(0,0,1;0rad)
  Width = 46.3
FEATURE [Part::Box] Box333  label="Krychle333"
  AttacherType = Attacher::AttachEngine3D
  Height = 12
  Length = 42.3
  Placement = pos=(-21.15,-21.15,-70) rot=(0,0,1;0rad)
  Width = 42.3
FEATURE [Part::Cut] Cut308
  Base = -> Box332
  Placement = pos=(17,-32,10) rot=(-1,0,0;1.5708rad)
  Tool = -> Box333
FEATURE [Part::Box] Box334  label="Krychle334"
  AttacherType = Attacher::AttachEngine3D
  Height = 12
  Length = 7
  Placement = pos=(-22,15,-74) rot=(0,0,1;0rad)
  Width = 7
FEATURE [Part::Cylinder] Cylinder512  label="Válec512"
  Angle = 360
  AttacherType = Attacher::AttachEngine3D
  Height = 12
  Placement = pos=(-15.15,15.15,-74) rot=(0,0,1;0rad)
  Radius = 6
FEATURE [Part::Cut] Cut309
  Base = -> Box334
  Placement = pos=(0,0,0) rot=(0,0,1;1.5708rad)
  Tool = -> Cylinder512
FEATURE [Part::Box] Box335  label="Krychle335"
  AttacherType = Attacher::AttachEngine3D
  Height = 36
  Length = 7.85
  Placement = pos=(-10,-134,-8) rot=(0,0,1;0rad)
  Width = 56
FEATURE [Part::Box] Box336  label="Krychle336"
  AttacherType = Attacher::AttachEngine3D
  Height = 36
  Length = 7.85
  Placement = pos=(36.15,-134,-8) rot=(0,0,1;0rad)
  Width = 56
FEATURE [Part::Box] Box337  label="Krychle337"
  AttacherType = Attacher::AttachEngine3D
  Height = 36
  Length = 7.85
  Placement = pos=(36.15,-134,-8) rot=(0,0,1;0rad)
  Width = 56
FEATURE [Part::Compound] Compound253
  Links = -> [Box335,Box336]
FEATURE [Part::Cut] Cut310
  Base = -> Box334
  Placement = pos=(0,0,0) rot=(0,0,-1;1.5708rad)
  Tool = -> Cylinder512
FEATURE [Part::Cut] Cut311
  Base = -> Box334
  Tool = -> Cylinder512
FEATURE [Part::Cut] Cut312
  Base = -> Box334
  Placement = pos=(0,0,0) rot=(0,0,1;3.14159rad)
  Tool = -> Cylinder512
FEATURE [Part::Compound] Compound251
  Links = -> [Cut311,Cut309,Cut312,Cut310]
  Placement = pos=(17,-28,10) rot=(-1,0,0;1.5708rad)
FEATURE [Part::Cut] Cut313
  Base = -> Compound251
  Tool = -> Compound253
FEATURE [Part::Cut] Cut315
  Base = -> Cut301
  Tool = -> Torus
FEATURE [Part::Box] Box338  label="Krychle338"
  AttacherType = Attacher::AttachEngine3D
  Height = 36
  Length = 7.85
  Placement = pos=(-10,-134,-8) rot=(0,0,1;0rad)
  Width = 56
FEATURE [Part::Compound] Compound254
  Links = -> [Box338,Box337]
FEATURE [Part::Cut] Cut314
  Base = -> Cut308
  Tool = -> Compound254
FEATURE [Part::Compound] Compound255
  Links = -> [Cut313,Cut314]
  Placement = pos=(0,-2,0) rot=(0,0,1;0rad)
FEATURE [Part::Cut] Cut316
  Base = -> Compound255
  Placement = pos=(0,-2,0) rot=(0,0,1;0rad)
  Tool = -> Torus001
FEATURE [Part::Cylinder] Cylinder2200  label="Válec2200"
  Angle = 360
  AttacherType = Attacher::AttachEngine3D
  Height = 10
  Placement = pos=(17,-98,44) rot=(1,0,0;1.5708rad)
  Radius = 2
FEATURE [Part::Cut] Cut803
  Base = -> Cut315
  Tool = -> Cylinder2200
FEATURE [Part::Box] Box849  label="Krychle848"
  AttacherType = Attacher::AttachEngine3D
  Height = 28
  Length = 2
  Placement = pos=(-12,-117,-4) rot=(0,0,1;0rad)
  Width = 14
FEATURE [Part::Box] Box898  label="Krychle897"
  AttacherType = Attacher::AttachEngine3D
  Height = 28
  Length = 2
  Placement = pos=(44,-117,-4) rot=(0,0,1;0rad)
  Width = 14
FEATURE [Part::Compound] Compound994  label="wrist_halo_inner2"
  Links = -> [Box849,Box898,Cut803]
  Placement = pos=(0,-2,0) rot=(0,0,1;0rad)
FEATURE [Part::Cylinder] Cylinder2224  label="Válec2224"
  Angle = 360
  AttacherType = Attacher::AttachEngine3D
  Height = 20
  Placement = pos=(-17,-108,2) rot=(0,1,0;1.5708rad)
  Radius = 1
FEATURE [Part::Cylinder] Cylinder2225  label="Válec2225"
  Angle = 360
  AttacherType = Attacher::AttachEngine3D
  Height = 20
  Placement = pos=(-17,-108,18) rot=(0,1,0;1.5708rad)
  Radius = 1
FEATURE [Part::Cylinder] Cylinder2226  label="Válec2226"
  Angle = 360
  AttacherType = Attacher::AttachEngine3D
  Height = 20
  Placement = pos=(32,-108,2) rot=(0,1,0;1.5708rad)
  Radius = 1
FEATURE [Part::Cylinder] Cylinder2227  label="Válec2227"
  Angle = 360
  AttacherType = Attacher::AttachEngine3D
  Height = 20
  Placement = pos=(32,-108,18) rot=(0,1,0;1.5708rad)
  Radius = 1
FEATURE [Part::Compound] Compound995  label="wrist_halo_inner003"
  Links = -> [Cut316,Compound994]
FEATURE [Part::Compound] Compound1007
  Links = -> [Cylinder2226,Cylinder2227]
  Placement = pos=(0,-3,0) rot=(0,0,1;0rad)
FEATURE [Part::Compound] Compound1008
  Links = -> [Cylinder2224,Cylinder2225]
  Placement = pos=(0,-3,0) rot=(0,0,1;0rad)
FEATURE [Part::Compound] Compound1011
  Links = -> [Compound1007,Compound1008]
  Placement = pos=(0,-1.5,0) rot=(0,0,1;0rad)
FEATURE [Part::Cut] Cut830  label="Wrist_inner-halo"
  Base = -> Compound995
  Placement = pos=(-17,10,111) rot=(1,0,0;1.5708rad)
  Tool = -> Compound1011
FEATURE [Mesh::Feature] Mesh  label="G-mini_encoder-ring-cover (Meshed)"
FEATURE [Mesh::Feature] Mesh001  label="Wrist_halo-cover (Meshed)"
FEATURE [Mesh::Feature] Mesh002  label="G-mini_encoder-ring-cover (Meshed)001"
FEATURE [Mesh::Feature] Mesh003  label="G-mini_encoder-belt-ring (Meshed)"
FEATURE [Mesh::Feature] Mesh004  label="Wrist_inner-halo (Meshed)"
